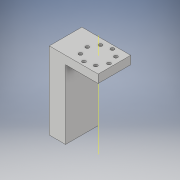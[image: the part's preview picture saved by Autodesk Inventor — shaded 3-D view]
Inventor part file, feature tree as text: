
AUTODESK INVENTOR PART (.ipt)
format: ipt  version: 2019 (Build 230136000, 136)  size: 121,344 bytes
history: native  units: in
note: dims shown in document units (in); Inventor stores cm internally (conversion verified against a paired STEP export)
features: sketch x2, extrude x1, hole x1, other x1
ambient origin geometry x8: Origin, YZ Plane, XZ Plane, XY Plane, X Axis, Y Axis, Z Axis, Center Point
bodies: Body1 (feature_tree)
feature tree (5):
  extrude  "Extrusion3"  Depth=0.25in
  hole  "Hole2"  [1 undecoded]
  other  "Work Axis1"
  sketch  "Sketch4"  dims[d25=2.371in d26=0.25in]
  sketch  "Sketch5"  dims[d27=1.0in d28=0.5in d29=1.0in d30=0.0in d34=3.1496in d36=360.0deg d38=0.107in d39=0.75in d40=0.375in d41=0.25in d42=0.5635in d43=1.0in d44=0.8108in d45=0.385in d46=0.5in d47=0.5in]
note: 1 required parameter value undecoded (feature->parameter linkage not recoverable at this tier; creation-order binding heuristic only, values carry confidence <= 0.55)
